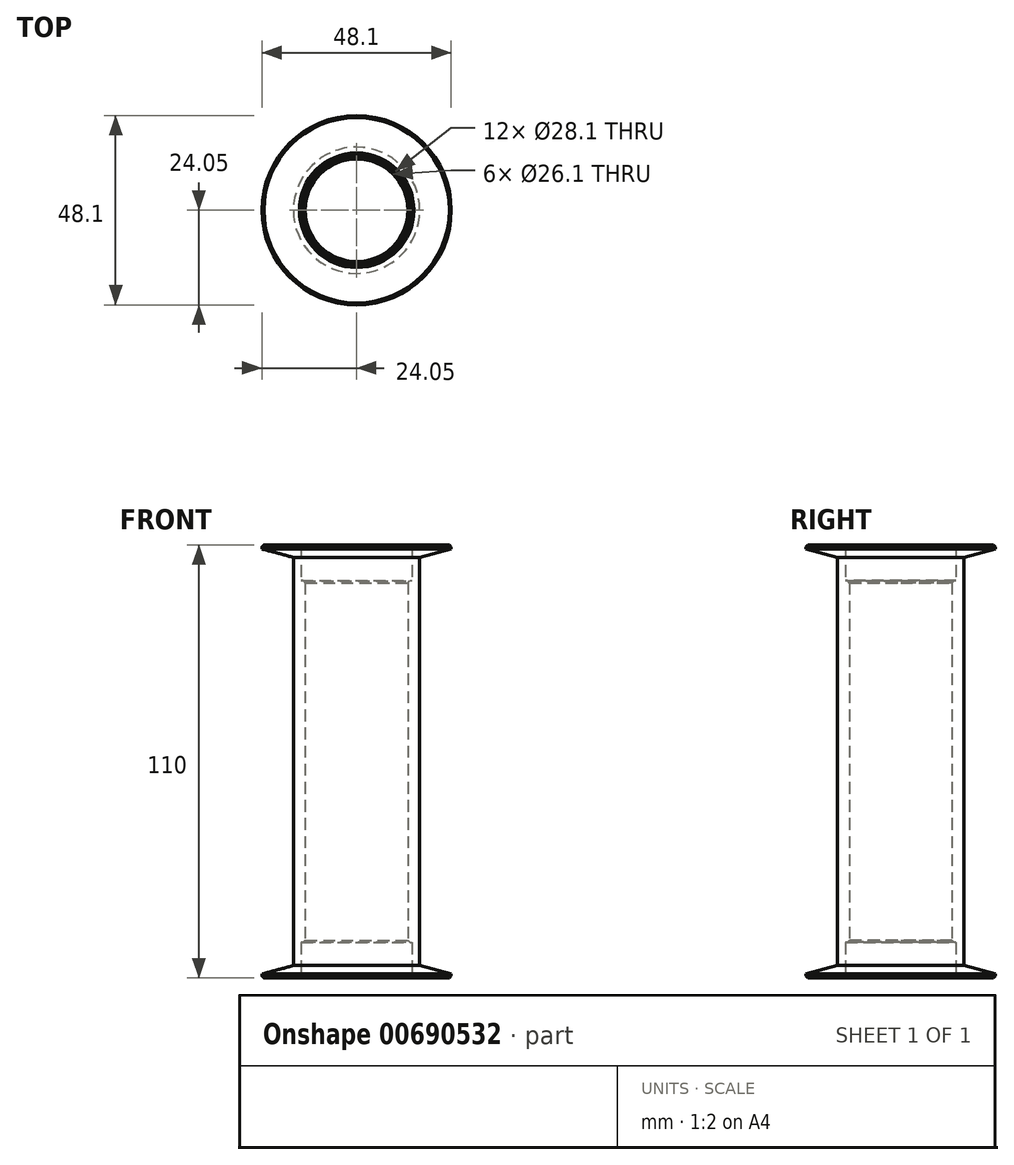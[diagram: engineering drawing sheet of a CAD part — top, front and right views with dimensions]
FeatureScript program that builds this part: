
annotation { "Feature Type Name" : "Feature", "Feature Type Description" : "" }
export const myFeature = defineFeature(function(context is Context, id is Id, definition is map)
    precondition{}
    {
        {
            var Q0;
            Q0=qCreatedBy(makeId("Front.planeOp"),FACE);
            var sketch = newSketch(context, id + "F0", { "sketchPlane" : qUnion([Q0])});
            skLineSegment(sketch, "E0", {"start": v(0, 0) * mm, "end": v(0, 75.93) * mm, "construction": true});
            skSolve(sketch);
        }
        {
            var Q0;
            Q0=qCreatedBy(makeId("Front.planeOp"),FACE);
            var sketch = newSketch(context, id + "F1", { "sketchPlane" : qUnion([Q0])});
            skLineSegment(sketch, "E1", {"start": v(-14.05, -55) * mm, "end": v(-24.05, -55) * mm});
            skLineSegment(sketch, "E2", {"start": v(-24.05, -55) * mm, "end": v(-24.05, -54) * mm});
            skLineSegment(sketch, "E3", {"start": v(-16.05, -51.86) * mm, "end": v(-16.05, 0) * mm});
            skLineSegment(sketch, "E4", {"start": v(-16.05, 0) * mm, "end": v(-13.05, 0) * mm});
            skLineSegment(sketch, "E5", {"start": v(-13.05, 0) * mm, "end": v(-13.05, -45.82) * mm});
            skLineSegment(sketch, "E6", {"start": v(-13.05, -45.82) * mm, "end": v(-14.05, -46) * mm});
            skLineSegment(sketch, "E7", {"start": v(-14.05, -46) * mm, "end": v(-14.05, -55) * mm});
            skPoint(sketch, "E8.orphan", {"position": v(0, -55) * mm});
            skPoint(sketch, "E9.visualSharp", {"position": v(-16.05, -49.5) * mm});
            skLineSegment(sketch, "E10.MirrorCS", {"start": v(-24.05, 55) * mm, "end": v(-24.05, 54) * mm});
            skLineSegment(sketch, "E11.MirrorCS", {"start": v(-13.05, 45.82) * mm, "end": v(-14.05, 46) * mm});
            skLineSegment(sketch, "E12.MirrorCS", {"start": v(-14.05, 55) * mm, "end": v(-24.05, 55) * mm});
            skLineSegment(sketch, "E13.MirrorCS", {"start": v(-24.05, 54) * mm, "end": v(-16.05, 51.86) * mm});
            skPoint(sketch, "E14.MirrorP", {"position": v(-16.05, 49.5) * mm});
            skLineSegment(sketch, "E15.MirrorCS", {"start": v(-13.05, 0) * mm, "end": v(-13.05, 45.82) * mm});
            skLineSegment(sketch, "E16.MirrorCS", {"start": v(-14.05, 46) * mm, "end": v(-14.05, 55) * mm});
            skLineSegment(sketch, "E17.MirrorCS", {"start": v(-16.05, 51.86) * mm, "end": v(-16.05, 0) * mm});
            skLineSegment(sketch, "E18", {"start": v(-24.05, -54) * mm, "end": v(-16.05, -51.86) * mm});
            skPoint(sketch, "E9.filletArc.end.orphan", {"position": v(-16.05, -48.5) * mm});
            skPoint(sketch, "E9.filletArc.start.orphan", {"position": v(-15.36, -51.67) * mm});
            skPoint(sketch, "E19.orphan", {"position": v(-15.36, 51.67) * mm});
            skPoint(sketch, "E20.orphan", {"position": v(-16.05, 48.5) * mm});
            skSolve(sketch);
        }
        {
            var Q0;
            Q0=makeQuery(id+"F1.imprint","IMPRINT",FACE,{"disambiguationData":[TD([[makeQuery(id+"F1.imprint","IMPRINT",EDGE,{"derivedFrom":sQuery(id+"F1.wireOp",EDGE,"E10.MirrorCS")}),1.0]])]});
            var Q1;
            Q1=makeQuery(id+"F1.imprint","IMPRINT",FACE,{"disambiguationData":[TD([[makeQuery(id+"F1.imprint","IMPRINT",EDGE,{"derivedFrom":sQuery(id+"F1.wireOp",EDGE,"E1")}),-1.0]])]});
            var Q2;
            Q2=sQuery(id+"F0.wireOp",EDGE,"E0");
            revolve(context, id + "F2", {"entities" : qUnion([Q0, Q1]), "axis" : qUnion([Q2]), "revolveType" : RevolveType.FULL});
        }
        {
            var Q0;
            Q0=makeQuery(id+"F2.opRevolve","SWEPT_EDGE",EDGE,{"disambiguationData":[OSD([sQuery(id+"F1.wireOp",EDGE,"E1"),sQuery(id+"F1.wireOp",EDGE,"E7")])]});
            var Q1;
            Q1=makeQuery(id+"F2.opRevolve","SWEPT_EDGE",EDGE,{"disambiguationData":[OSD([sQuery(id+"F1.wireOp",EDGE,"E12.MirrorCS"),sQuery(id+"F1.wireOp",EDGE,"E16.MirrorCS")])]});
            var Q2;
            Q2=makeQuery(id+"F2.opRevolve","SWEPT_EDGE",EDGE,{"disambiguationData":[OSD([sQuery(id+"F1.wireOp",EDGE,"E1"),sQuery(id+"F1.wireOp",EDGE,"E2")])]});
            var Q3;
            Q3=makeQuery(id+"F2.opRevolve","SWEPT_EDGE",EDGE,{"disambiguationData":[OSD([sQuery(id+"F1.wireOp",EDGE,"E10.MirrorCS"),sQuery(id+"F1.wireOp",EDGE,"E12.MirrorCS")])]});
            chamfer(context, id + "F3", {"entities" : qUnion([Q0, Q1, Q2, Q3]), "width" : 0.5 * mm, "tangentPropagation" : true});
        }
        {
            var Q0;
            Q0=makeQuery(id+"F2.opRevolve","SWEPT_EDGE",EDGE,{"disambiguationData":[OSD([sQuery(id+"F1.wireOp",EDGE,"E11.MirrorCS"),sQuery(id+"F1.wireOp",EDGE,"E15.MirrorCS")])]});
            var Q1;
            Q1=makeQuery(id+"F2.opRevolve","SWEPT_EDGE",EDGE,{"disambiguationData":[OSD([sQuery(id+"F1.wireOp",EDGE,"E5"),sQuery(id+"F1.wireOp",EDGE,"E6")])]});
            chamfer(context, id + "F4", {"entities" : qUnion([Q0, Q1]), "width" : 0.5 * mm, "tangentPropagation" : true});
        }
    });
